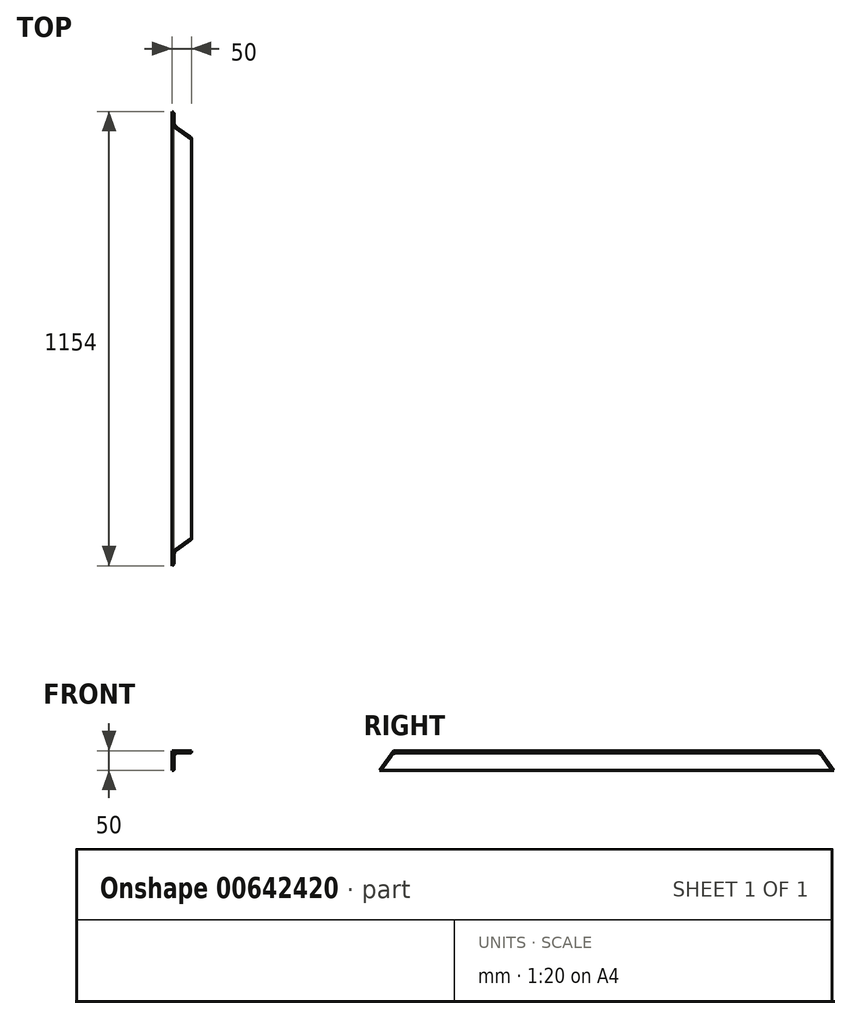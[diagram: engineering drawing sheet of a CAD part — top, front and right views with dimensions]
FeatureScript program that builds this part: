
annotation { "Feature Type Name" : "Feature", "Feature Type Description" : "" }
export const myFeature = defineFeature(function(context is Context, id is Id, definition is map)
    precondition{}
    {
        {
            var Q0;
            Q0=qCreatedBy(makeId("Front.planeOp"),FACE);
            var sketch = newSketch(context, id + "F0", { "sketchPlane" : qUnion([Q0])});
            skLineSegment(sketch, "E0", {"start": v(-9.45, -21.6) * mm, "end": v(-9.45, 28.4) * mm});
            skLineSegment(sketch, "E1", {"start": v(-9.45, 28.4) * mm, "end": v(40.55, 28.4) * mm});
            skLineSegment(sketch, "E2.0", {"start": v(3.55, 22.4) * mm, "end": v(37.05, 22.4) * mm});
            skLineSegment(sketch, "E2.1", {"start": v(-3.45, -18.1) * mm, "end": v(-3.45, 15.4) * mm});
            skPoint(sketch, "E3.visualSharp", {"position": v(-3.45, 22.4) * mm});
            skArc(sketch, "E3.filletArc", {"start": v(3.55, 22.4) * mm, "mid": v(-1.4, 20.35) * mm, "end": v(-3.45, 15.4) * mm});
            skLineSegment(sketch, "E4", {"start": v(40.55, 28.4) * mm, "end": v(40.55, 25.9) * mm});
            skLineSegment(sketch, "E5", {"start": v(-9.45, -21.6) * mm, "end": v(-6.95, -21.6) * mm});
            skPoint(sketch, "E6.visualSharp", {"position": v(40.55, 22.4) * mm});
            skArc(sketch, "E6.filletArc", {"start": v(37.05, 22.4) * mm, "mid": v(39.52, 23.43) * mm, "end": v(40.55, 25.9) * mm});
            skPoint(sketch, "E7.visualSharp", {"position": v(-3.45, -21.6) * mm});
            skArc(sketch, "E7.filletArc", {"start": v(-6.95, -21.6) * mm, "mid": v(-4.48, -20.57) * mm, "end": v(-3.45, -18.1) * mm});
            skSolve(sketch);
        }
        {
            var Q0;
            Q0=makeQuery(id+"F0.imprint","IMPRINT",FACE,{"disambiguationData":[TD([[makeQuery(id+"F0.imprint","IMPRINT",EDGE,{"derivedFrom":sQuery(id+"F0.wireOp",EDGE,"E0")}),-1.0]])]});
            extrude(context, id + "F1", {"entities" : qUnion([Q0]), "depth" : 1154 * mm, "offsetDistance" : 25 * mm});
        }
        {
            var Q0;
            Q0=makeQuery(id+"F1.opExtrude","CAP_EDGE",EDGE,{"disambiguationData":[OSD([sQuery(id+"F0.wireOp",EDGE,"E6.filletArc")])],"isStart":false});
            cPoint(context, id + "F2", {"entities" : qUnion([Q0]), "parameter" : 0.5});
        }
        {
            var Q0;
            Q0=makeQuery(id+"F1.opExtrude","CAP_EDGE",EDGE,{"disambiguationData":[OSD([sQuery(id+"F0.wireOp",EDGE,"E7.filletArc")])],"isStart":false});
            cPoint(context, id + "F3", {"entities" : qUnion([Q0]), "parameter" : 0.5});
        }
        {
            var Q0;
            Q0=makeQuery(id+"F1.opExtrude","CAP_EDGE",EDGE,{"disambiguationData":[OSD([sQuery(id+"F0.wireOp",EDGE,"E6.filletArc")])],"isStart":true});
            cPoint(context, id + "F4", {"entities" : qUnion([Q0]), "parameter" : 0.5});
        }
        {
            var Q0;
            Q0 = qCreatedBy(id + "F2" ,VERTEX);
            var Q1;
            Q1 = qCreatedBy(id + "F3" ,VERTEX);
            var Q2;
            Q2 = qCreatedBy(id + "F4" ,VERTEX);
            cPlane(context, id + "F5", {"entities" : qUnion([Q0, Q1, Q2]), "cplaneType" : CPlaneType.THREE_POINT, "offset" : 25 * mm, "width" : 150 * mm, "height" : 150 * mm});
        }
        {
            var Q0;
            Q0=qCreatedBy(id+"F5.planeOp",FACE);
            var sketch = newSketch(context, id + "F6", { "sketchPlane" : qUnion([Q0])});
            skPoint(sketch, "E8.0", {"position": v(0, -21.96) * mm});
            skLineSegment(sketch, "E9", {"start": v(0, -21.96) * mm, "end": v(70.71, 48.75) * mm});
            skLineSegment(sketch, "E10", {"start": v(70.71, 48.75) * mm, "end": v(0, 48.75) * mm});
            skLineSegment(sketch, "E11", {"start": v(0, 48.75) * mm, "end": v(0, -21.96) * mm});
            skSolve(sketch);
        }
        {
            var Q0;
            Q0=makeQuery(id+"F6.imprint","IMPRINT",FACE,{"disambiguationData":[TD([[makeQuery(id+"F6.imprint","IMPRINT",EDGE,{"derivedFrom":sQuery(id+"F6.wireOp",EDGE,"E9")}),1.0]])]});
            extrude(context, id + "F7", {"entities" : qUnion([Q0]), "operationType" : NewBodyOperationType.REMOVE, "depth" : 45 * mm, "offsetDistance" : 25 * mm});
        }
        {
            var Q0;
            Q0=qCreatedBy(id+"F5.planeOp",FACE);
            var sketch = newSketch(context, id + "F8", { "sketchPlane" : qUnion([Q0])});
            skPoint(sketch, "E12.0", {"position": v(1154, -21.96) * mm});
            skLineSegment(sketch, "E13", {"start": v(1154, -21.96) * mm, "end": v(1083.29, 48.75) * mm});
            skLineSegment(sketch, "E14", {"start": v(1083.29, 48.75) * mm, "end": v(1154, 48.75) * mm});
            skLineSegment(sketch, "E15", {"start": v(1154, 48.75) * mm, "end": v(1154, -21.96) * mm});
            skSolve(sketch);
        }
        {
            var Q0;
            Q0=makeQuery(id+"F8.imprint","IMPRINT",FACE,{"disambiguationData":[TD([[makeQuery(id+"F8.imprint","IMPRINT",EDGE,{"derivedFrom":sQuery(id+"F8.wireOp",EDGE,"E13")}),-1.0]])]});
            extrude(context, id + "F9", {"entities" : qUnion([Q0]), "operationType" : NewBodyOperationType.REMOVE, "depth" : 45 * mm, "offsetDistance" : 25 * mm});
        }
        {
            var Q0;
            Q0=makeQuery(id+"F1.opExtrude","SWEPT_EDGE",EDGE,{"disambiguationData":[OSD([sQuery(id+"F0.wireOp",EDGE,"E0"),sQuery(id+"F0.wireOp",EDGE,"E5")])]});
            var Q1;
            Q1=qCreatedBy(id+"F5.planeOp",FACE);
            cPlane(context, id + "F10", {"entities" : qUnion([Q0, Q1]), "cplaneType" : CPlaneType.LINE_ANGLE, "offset" : 25 * mm, "angle" : 90 * degree, "width" : 150 * mm, "height" : 150 * mm});
        }
        {
            var Q0;
            Q0=qCreatedBy(id+"F10.planeOp",FACE);
            var sketch = newSketch(context, id + "F11", { "sketchPlane" : qUnion([Q0])});
            skLineSegment(sketch, "E16.bottom", {"start": v(6.2, -2) * mm, "end": v(11.02, -2) * mm});
            skLineSegment(sketch, "E16.top", {"start": v(6.2, 1156.32) * mm, "end": v(11.02, 1156.32) * mm});
            skLineSegment(sketch, "E16.left", {"start": v(6.2, -2) * mm, "end": v(6.2, 1156.32) * mm});
            skLineSegment(sketch, "E16.right", {"start": v(11.02, -2) * mm, "end": v(11.02, 1156.32) * mm});
            skSolve(sketch);
        }
        {
            var Q0;
            Q0=makeQuery(id+"F11.imprint","IMPRINT",FACE,{"disambiguationData":[TD([[makeQuery(id+"F11.imprint","IMPRINT",EDGE,{"derivedFrom":sQuery(id+"F11.wireOp",EDGE,"E16.bottom")}),1.0]])]});
            extrude(context, id + "F12", {"entities" : qUnion([Q0]), "operationType" : NewBodyOperationType.REMOVE, "oppositeDirection" : true, "depth" : 0.5 * mm, "offsetDistance" : 25 * mm});
        }
    });
